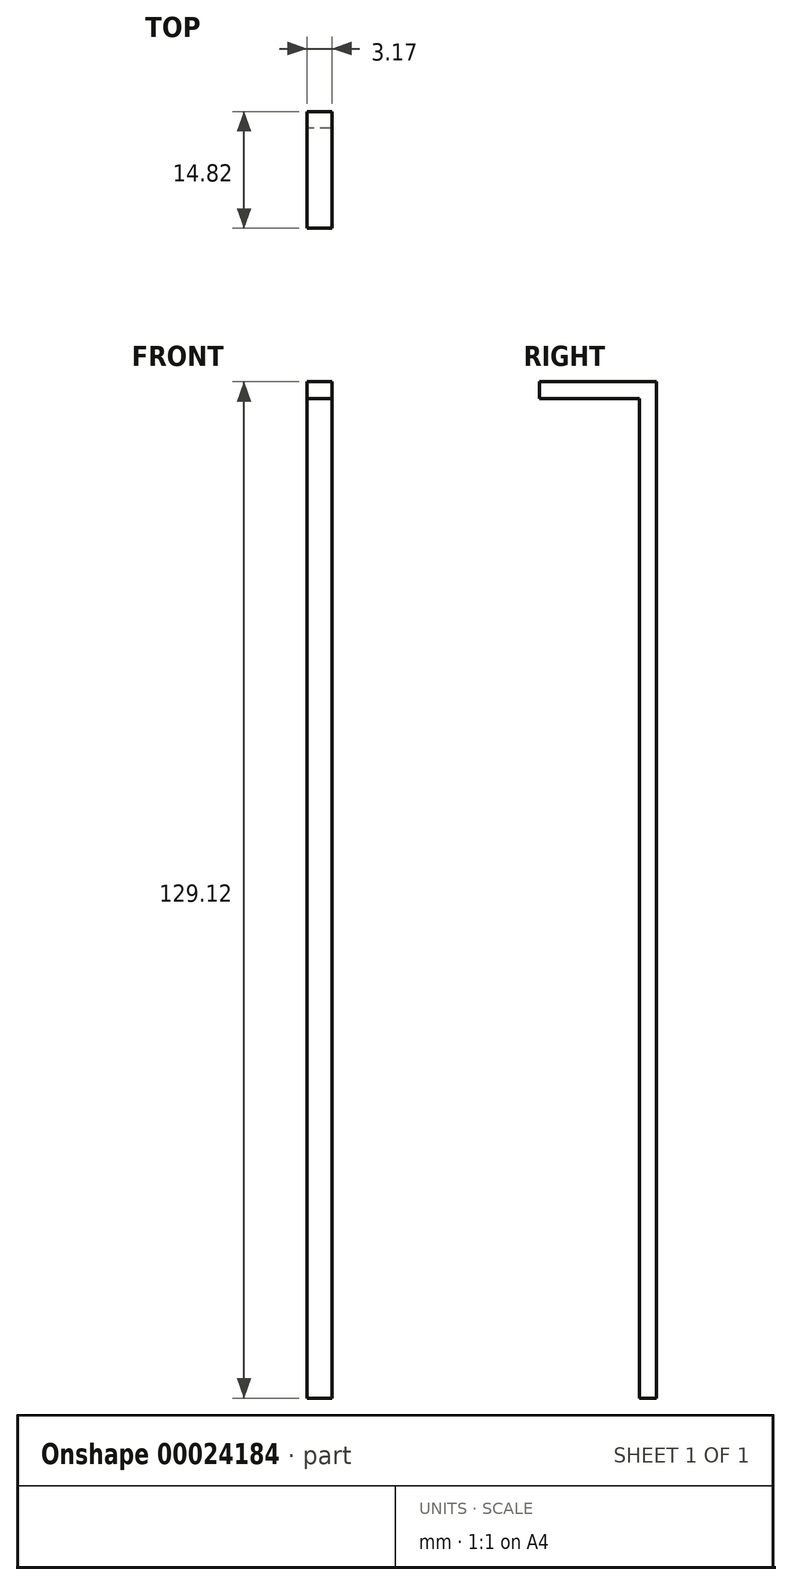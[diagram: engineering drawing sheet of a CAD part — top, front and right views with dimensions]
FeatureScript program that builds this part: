
annotation { "Feature Type Name" : "Feature", "Feature Type Description" : "" }
export const myFeature = defineFeature(function(context is Context, id is Id, definition is map)
    precondition{}
    {
        {
            var Q0;
            Q0=qCreatedBy(makeId("Right.planeOp"),FACE);
            var sketch = newSketch(context, id + "F0", { "sketchPlane" : qUnion([Q0])});
            skLineSegment(sketch, "E0", {"start": v(0, 0) * mm, "end": v(2.12, 0) * mm});
            skLineSegment(sketch, "E1", {"start": v(0, 0) * mm, "end": v(0, 127) * mm});
            skLineSegment(sketch, "E2", {"start": v(0, 127) * mm, "end": v(-12.7, 127) * mm});
            skLineSegment(sketch, "E3", {"start": v(-12.7, 127) * mm, "end": v(-12.7, 129.12) * mm});
            skLineSegment(sketch, "E4", {"start": v(-12.7, 129.12) * mm, "end": v(2.12, 129.12) * mm});
            skLineSegment(sketch, "E5", {"start": v(2.12, 129.12) * mm, "end": v(2.12, 0) * mm});
            skSolve(sketch);
        }
        {
            var Q0;
            Q0 = qSketchRegion(id + "F0", true);
            extrude(context, id + "F1", {"entities" : qUnion([Q0]), "depth" : 3.17 * mm});
        }
    });
